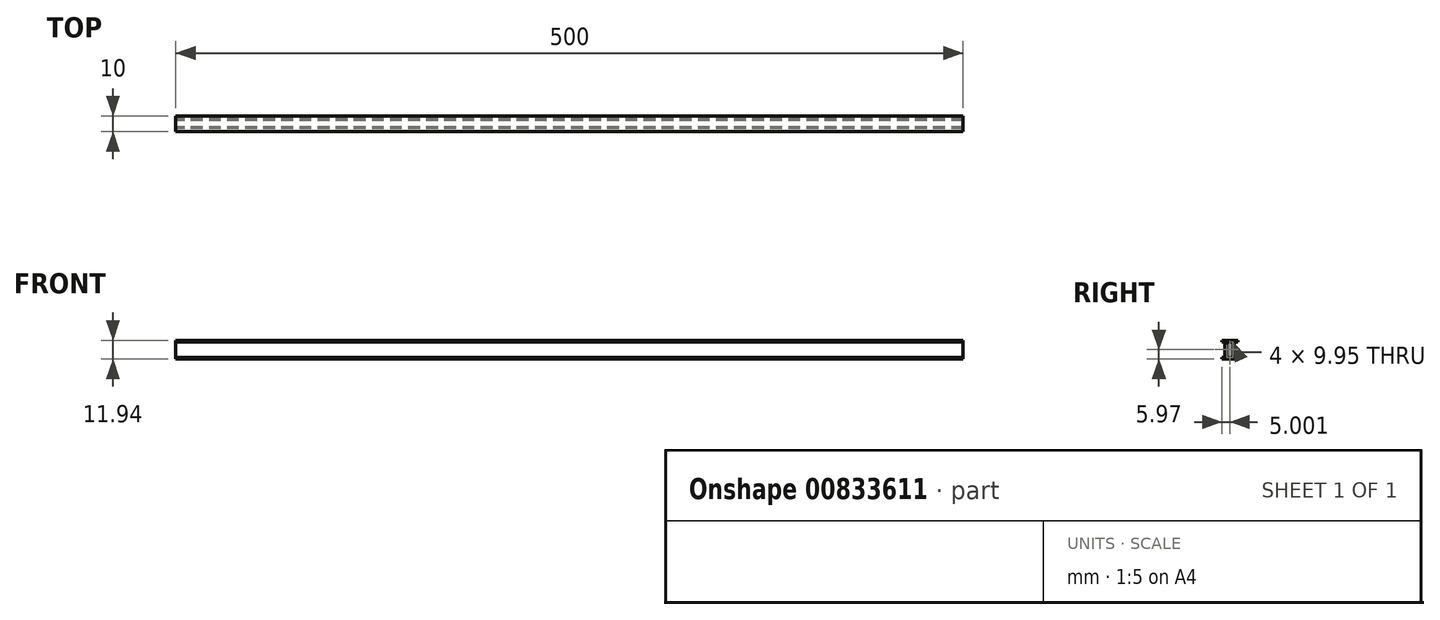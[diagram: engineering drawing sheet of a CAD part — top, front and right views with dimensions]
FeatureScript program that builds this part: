
annotation { "Feature Type Name" : "Feature", "Feature Type Description" : "" }
export const myFeature = defineFeature(function(context is Context, id is Id, definition is map)
    precondition{}
    {
        {
            var Q0;
            Q0=qCreatedBy(makeId("Right.planeOp"),FACE);
            var sketch = newSketch(context, id + "F0", { "sketchPlane" : qUnion([Q0])});
            skLineSegment(sketch, "E0", {"start": v(-33.48, 22.05) * mm, "end": v(-23.48, 22.05) * mm});
            skLineSegment(sketch, "E1", {"start": v(-33.48, 22.05) * mm, "end": v(-33.48, 21.05) * mm});
            skLineSegment(sketch, "E2", {"start": v(-23.48, 21.05) * mm, "end": v(-23.48, 22.05) * mm});
            skLineSegment(sketch, "E3", {"start": v(-33.48, 11.1) * mm, "end": v(-33.48, 10.1) * mm});
            skLineSegment(sketch, "E4", {"start": v(-33.48, 10.1) * mm, "end": v(-23.48, 10.1) * mm});
            skLineSegment(sketch, "E5", {"start": v(-23.48, 10.1) * mm, "end": v(-23.48, 11.1) * mm});
            skLineSegment(sketch, "E6", {"start": v(-33.48, 21.05) * mm, "end": v(-31.48, 21.05) * mm});
            skLineSegment(sketch, "E7", {"start": v(-31.48, 21.05) * mm, "end": v(-31.48, 11.1) * mm});
            skLineSegment(sketch, "E8", {"start": v(-31.48, 11.1) * mm, "end": v(-33.48, 11.1) * mm});
            skLineSegment(sketch, "E9", {"start": v(-23.48, 21.05) * mm, "end": v(-25.48, 21.05) * mm});
            skLineSegment(sketch, "E10", {"start": v(-25.48, 21.05) * mm, "end": v(-25.48, 11.1) * mm});
            skLineSegment(sketch, "E11", {"start": v(-25.48, 11.1) * mm, "end": v(-23.48, 11.1) * mm});
            skLineSegment(sketch, "E12", {"start": v(-26.48, 21.05) * mm, "end": v(-26.48, 11.1) * mm});
            skLineSegment(sketch, "E13", {"start": v(-26.48, 11.1) * mm, "end": v(-30.48, 11.1) * mm});
            skLineSegment(sketch, "E14", {"start": v(-30.48, 11.1) * mm, "end": v(-30.48, 21.05) * mm});
            skLineSegment(sketch, "E15", {"start": v(-30.48, 21.05) * mm, "end": v(-26.48, 21.05) * mm});
            skPoint(sketch, "E16", {"position": v(-28.48, 22.05) * mm});
            skLineSegment(sketch, "E17", {"start": v(-28.48, 32.32) * mm, "end": v(-28.48, 3.1) * mm, "construction": true});
            skSolve(sketch);
        }
        {
            var Q0;
            Q0=makeQuery(id+"F0.imprint","IMPRINT",FACE,{"disambiguationData":[TD([[makeQuery(id+"F0.imprint","IMPRINT",EDGE,{"derivedFrom":sQuery(id+"F0.wireOp",EDGE,"E0")}),-1.0]])]});
            extrude(context, id + "F1", {"entities" : qUnion([Q0]), "depth" : 500 * mm, "offsetDistance" : 25 * mm});
        }
        {
            var Q0;
            Q0=makeQuery(id+"F1.opExtrude","CAP_EDGE",EDGE,{"disambiguationData":[OSD([sQuery(id+"F0.wireOp",EDGE,"E12")])],"isStart":false});
            cPoint(context, id + "F2", {"entities" : qUnion([Q0]), "parameter" : 0.5});
        }
        {
            var Q0;
            Q0=makeQuery(id+"F1.opExtrude","CAP_EDGE",EDGE,{"disambiguationData":[OSD([sQuery(id+"F0.wireOp",EDGE,"E14")])],"isStart":false});
            cPoint(context, id + "F3", {"entities" : qUnion([Q0]), "parameter" : 0.5});
        }
        {
            var Q0;
            Q0 = qCreatedBy(id + "F2" ,VERTEX);
            var Q1;
            Q1 = qCreatedBy(id + "F3" ,VERTEX);
            cPlane(context, id + "F4", {"entities" : qUnion([Q0, Q1]), "cplaneType" : CPlaneType.MID_PLANE, "offset" : 25 * mm, "width" : 150 * mm, "height" : 150 * mm});
        }
    });
